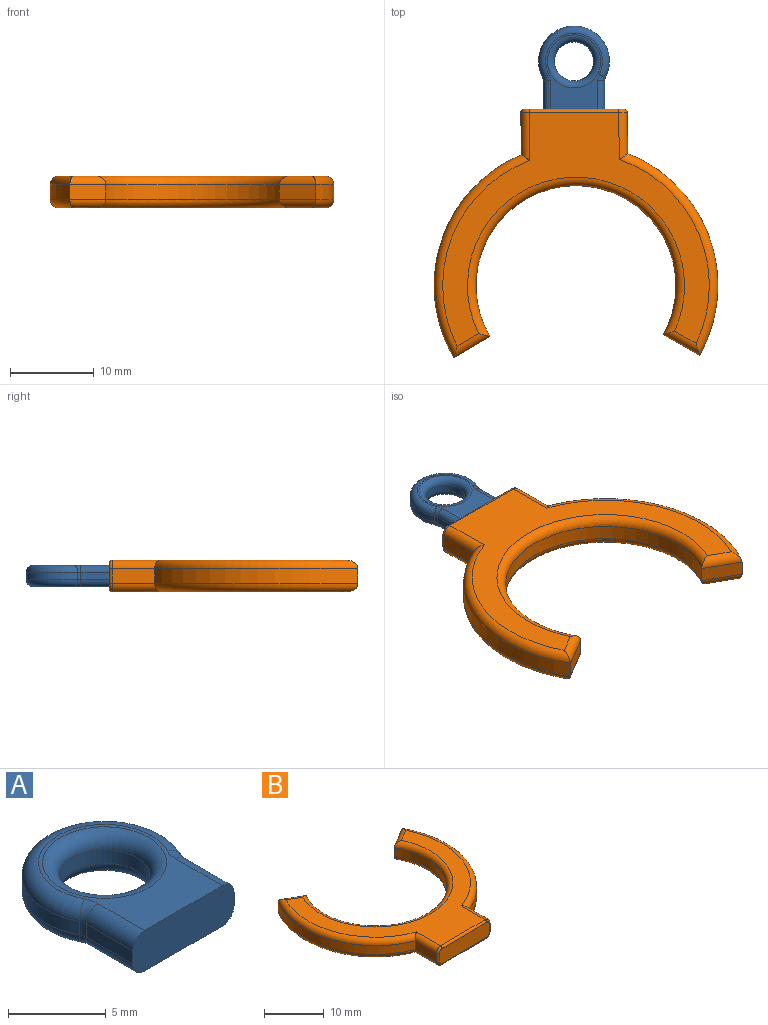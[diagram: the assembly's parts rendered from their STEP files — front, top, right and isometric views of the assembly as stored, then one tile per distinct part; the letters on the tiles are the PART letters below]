
ASSEMBLY  parts=2 mates=1
PART A: 21 faces, bbox 9.2x10.3x2.5 mm
  f0: plane 3.38x0.85mm, normal (1,0,0), area 2.9mm2, adj f3,f7,f11,f12
  f1: cylinder r=4.23mm len=8.47mm, axis (0,0,-1), area 14.7mm2, adj f10,f11,f15,f16
  f2: plane 3.38x0.85mm, normal (-1,0,0), area 2.9mm2, adj f3,f9,f15,f18
  f3: plane 7.33x2.54mm, normal (0,-1,0), area 18mm2, adj f0,f2,f5,f6,f7,f9,f12,f18
  f4: cylinder r=2.33mm len=4.66mm, axis (0,0,-1), area 12.4mm2, adj f19,f20
  f5: plane 9.1x6.77mm, normal (0,0,1), area 20.1mm2, adj f3,f12,f14,f16,f17,f18,f20
  f6: plane 9.1x6.77mm, normal (0,0,-1), area 20.1mm2, adj f3,f7,f8,f9,f10,f13,f19
  f7: cylinder r=0.85mm len=3.38mm, axis (0,1,0), area 4.5mm2, adj f0,f3,f6,f8
  f8: torus R=1.69mm, axis (0,0,1), area 0.7mm2, adj f6,f7,f10,f11
  f9: cylinder r=0.85mm len=3.38mm, axis (0,-1,0), area 4.5mm2, adj f2,f3,f6,f13
  f10: torus R=3.39mm, axis (0,0,1), area 21.4mm2, adj f1,f6,f8,f13
  f11: cylinder r=0.85mm len=0.85mm, axis (0,0,-1), area 0.3mm2, adj f0,f1,f8,f14
  f12: cylinder r=0.85mm len=3.38mm, axis (0,-1,0), area 4.5mm2, adj f0,f3,f5,f14
  f13: torus R=1.69mm, axis (0,0,1), area 0.7mm2, adj f6,f9,f10,f15
  f14: torus R=1.69mm, axis (0,0,1), area 0.7mm2, adj f5,f11,f12,f16
  f15: cylinder r=0.85mm len=0.85mm, axis (0,0,-1), area 0.3mm2, adj f1,f2,f13,f17
  f16: torus R=3.39mm, axis (0,0,1), area 21.4mm2, adj f1,f5,f14,f17
  f17: torus R=1.69mm, axis (0,0,1), area 0.7mm2, adj f5,f15,f16,f18
  f18: cylinder r=0.85mm len=3.38mm, axis (0,1,0), area 4.5mm2, adj f2,f3,f5,f17
  f19: torus R=3.17mm, axis (0,0,1), area 22mm2, adj f4,f6
  f20: torus R=3.17mm, axis (0,0,1), area 22mm2, adj f4,f5
PART B: 32 faces, bbox 36.7x30.3x3.8 mm
  f0: plane 31.83x27.81mm, normal (0,0,1), area 227.3mm2, adj f16,f17,f18,f19,f20,f21,f22,f25
  f1: plane 4.92x1.78mm, normal (1,0,0), area 8.8mm2, adj f2,f13,f20,f26
  f2: cylinder r=16.93mm len=24.16mm, axis (0,0,-1), area 51.5mm2, adj f1,f3,f11,f18
  f3: plane 4.33x2.5mm, normal (-0.5,0.87,0), area 8.9mm2, adj f2,f4,f9,f16
  f4: cylinder r=11.94mm len=23.88mm, axis (0,0,-1), area 88.9mm2, adj f3,f5,f10,f17
  f5: plane 4.33x2.5mm, normal (0.5,0.87,0), area 8.9mm2, adj f4,f6,f12,f19
  f6: cylinder r=16.93mm len=24.16mm, axis (0,0,-1), area 51.5mm2, adj f5,f7,f14,f21
  f7: plane 5.06x1.78mm, normal (-1,0,0), area 9mm2, adj f6,f15,f22,f29
  f8: plane 31.83x27.81mm, normal (0,0,-1), area 227.3mm2, adj f9,f10,f11,f12,f13,f14,f15,f30
  f9: cylinder r=1.02mm len=4.83mm, axis (-0.87,-0.5,0), area 6.8mm2, adj f3,f8,f10,f11
  f10: torus R=12.95mm, axis (0,0,1), area 81.1mm2, adj f4,f8,f9,f12
  f11: torus R=15.92mm, axis (0,0,1), area 45mm2, adj f2,f8,f9,f13
  f12: cylinder r=1.02mm len=4.83mm, axis (-0.87,0.5,0), area 6.8mm2, adj f5,f8,f10,f14
  f13: cylinder r=1.02mm len=5.63mm, axis (0,1,0), area 8.3mm2, adj f1,f8,f11,f28
  f14: torus R=15.92mm, axis (0,0,1), area 45mm2, adj f6,f8,f12,f15
  f15: cylinder r=1.02mm len=5.76mm, axis (0,-1,0), area 8.5mm2, adj f7,f8,f14,f31
  f16: cylinder r=1.02mm len=4.83mm, axis (0.87,0.5,0), area 6.8mm2, adj f0,f3,f17,f18
  f17: torus R=12.95mm, axis (0,0,1), area 81.1mm2, adj f0,f4,f16,f19
  f18: torus R=15.92mm, axis (0,0,1), area 45mm2, adj f0,f2,f16,f20
  f19: cylinder r=1.02mm len=4.83mm, axis (0.87,-0.5,0), area 6.8mm2, adj f0,f5,f17,f21
  f20: cylinder r=1.02mm len=5.63mm, axis (0,-1,0), area 8.3mm2, adj f0,f1,f18,f24
  f21: torus R=15.92mm, axis (0,0,1), area 45mm2, adj f0,f6,f19,f22
  f22: cylinder r=1.02mm len=5.76mm, axis (0,1,0), area 8.5mm2, adj f0,f7,f21,f27
  f23: plane 11.96x3.07mm, normal (0.01,-1,0), area 36.4mm2, adj f24,f25,f26,f27,f28,f29,f30,f31
  f24: bspline ~1.19x1.19mm, area 0.8mm2, adj f20,f23,f25,f26
  f25: cylinder r=0.37mm len=10.67mm, axis (1,0.01,0), area 6.2mm2, adj f0,f23,f24,f27
  f26: cylinder r=0.37mm len=1.78mm, axis (0,0,1), area 1mm2, adj f1,f23,f24,f28
  f27: bspline ~1.2x1.06mm, area 0.8mm2, adj f22,f23,f25,f29
  f28: bspline ~1.02x1.02mm, area 0.8mm2, adj f13,f23,f26,f30
  f29: cylinder r=0.37mm len=1.78mm, axis (0,0,-1), area 1mm2, adj f7,f23,f27,f31
  f30: cylinder r=0.37mm len=10.67mm, axis (1,0.01,0), area 6.2mm2, adj f8,f23,f28,f31
  f31: bspline ~1.02x1.02mm, area 0.8mm2, adj f15,f23,f29,f30
PLACE A t=(25.9,3.92,-18.93)mm
PLACE B rot(axis=(1,0.01,0),180deg) t=(-91.55,-24.18,-17.66)mm
MATE fastened B.f23 <-> A.f3  axis (0,1,0) through (25.9,-1.79,-17.66)mm
